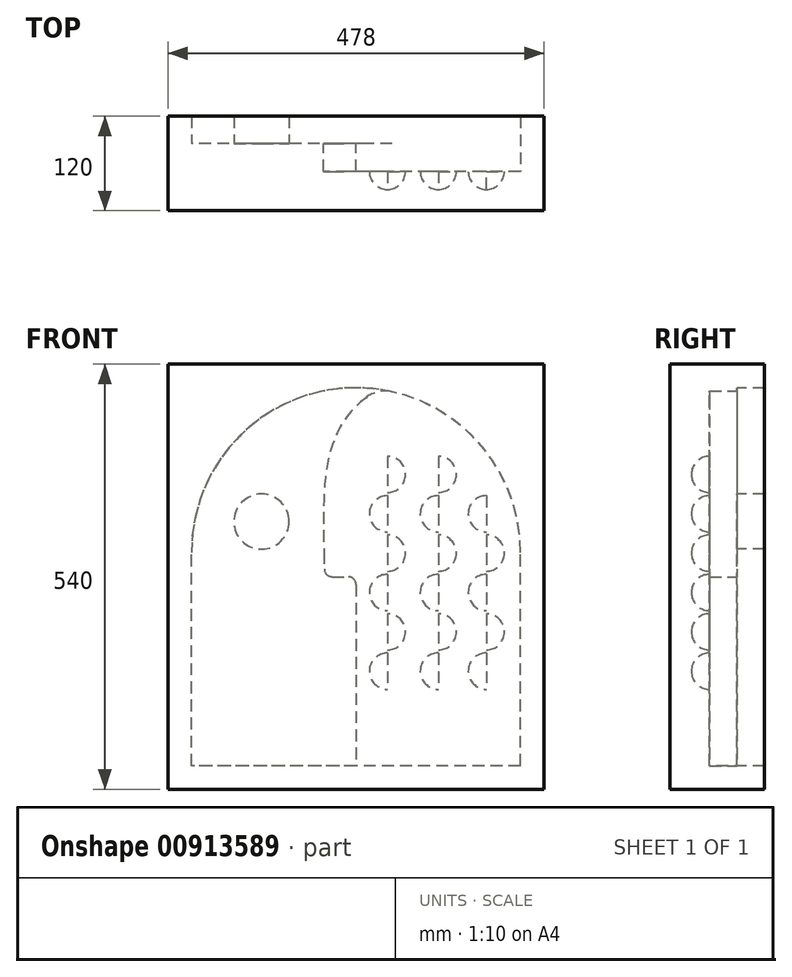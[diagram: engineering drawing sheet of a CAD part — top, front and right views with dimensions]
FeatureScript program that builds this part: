
annotation { "Feature Type Name" : "Feature", "Feature Type Description" : "" }
export const myFeature = defineFeature(function(context is Context, id is Id, definition is map)
    precondition{}
    {
        {
            var Q0;
            Q0=qCreatedBy(makeId("Front.planeOp"),FACE);
            var sketch = newSketch(context, id + "F0", { "sketchPlane" : qUnion([Q0])});
            skLineSegment(sketch, "E0.bottom", {"start": v(209, -110) * mm, "end": v(-209, -110) * mm});
            skLineSegment(sketch, "E0.top", {"start": v(209, 161) * mm, "end": v(-209, 161) * mm});
            skLineSegment(sketch, "E0.left", {"start": v(209, -110) * mm, "end": v(209, 161) * mm});
            skLineSegment(sketch, "E0.right", {"start": v(-209, -110) * mm, "end": v(-209, 161) * mm});
            skPoint(sketch, "E0.middle", {"position": v(0, 25.5) * mm});
            skArc(sketch, "E1", {"start": v(209, 161) * mm, "mid": v(0, 370) * mm, "end": v(-209, 161) * mm});
            skPoint(sketch, "E2.2.internal.snap0", {"position": v(0, 370) * mm});
            skFitSpline(sketch, "E3", {"points": [v(27.95, 368.12) * mm, v(-40, 130) * mm], "startDerivative": vector(-229.22, -141.56) * mm, "endDerivative": vector(8.15, -359.94) * mm});
            skLineSegment(sketch, "E4", {"start": v(-40, 130) * mm, "end": v(0, 130) * mm});
            skLineSegment(sketch, "E5", {"start": v(0, 130) * mm, "end": v(0, -110) * mm});
            skSolve(sketch);
        }
        {
            var Q0;
            {var subQ0=sQuery(id+"F0.wireOp",EDGE,"E1");var subQ3=sQuery(id+"F0.wireOp",EDGE,"E3");var subQ5=makeQuery(id+"F0.imprint","INTERSECT",VERTEX,{"derivedFrom":[subQ0,subQ3]});Q0=makeQuery(id+"F0.imprint","IMPRINT",FACE,{"disambiguationData":[TD([[makeQuery(id+"F0.imprint","IMPRINT",EDGE,{"disambiguationData":[TD([[subQ5,-1.0]])],"derivedFrom":subQ3}),1.0]])]});}
            var Q1;
            {var subQ4=sQuery(id+"F0.wireOp",EDGE,"E0.left");Q1=makeQuery(id+"F0.imprint","IMPRINT",FACE,{"disambiguationData":[TD([[makeQuery(id+"F0.imprint","IMPRINT",EDGE,{"derivedFrom":subQ4}),1.0]])]});}
            extrude(context, id + "F1", {"entities" : qUnion([Q0, Q1]), "depth" : 35 * mm, "offsetDistance" : 25 * mm});
        }
        {
            var Q0;
            {var subQ0=sQuery(id+"F0.wireOp",EDGE,"E1");var subQ3=sQuery(id+"F0.wireOp",EDGE,"E3");var subQ5=makeQuery(id+"F0.imprint","INTERSECT",VERTEX,{"derivedFrom":[subQ0,subQ3]});Q0=makeQuery(id+"F0.imprint","IMPRINT",FACE,{"disambiguationData":[TD([[makeQuery(id+"F0.imprint","IMPRINT",EDGE,{"disambiguationData":[TD([[subQ5,-1.0]])],"derivedFrom":subQ3}),-1.0]])]});}
            var Q1;
            {var subQ4=sQuery(id+"F0.wireOp",EDGE,"E0.right");Q1=makeQuery(id+"F0.imprint","IMPRINT",FACE,{"disambiguationData":[TD([[makeQuery(id+"F0.imprint","IMPRINT",EDGE,{"derivedFrom":subQ4}),-1.0]])]});}
            var Q2;
            {var subQ0=sQuery(id+"F0.wireOp",EDGE,"E1");var subQ3=sQuery(id+"F0.wireOp",EDGE,"E3");var subQ5=makeQuery(id+"F0.imprint","INTERSECT",VERTEX,{"derivedFrom":[subQ0,subQ3]});Q2=makeQuery(id+"F0.imprint","IMPRINT",FACE,{"disambiguationData":[TD([[makeQuery(id+"F0.imprint","IMPRINT",EDGE,{"disambiguationData":[TD([[subQ5,-1.0]])],"derivedFrom":subQ3}),1.0]])]});}
            var Q3;
            {var subQ4=sQuery(id+"F0.wireOp",EDGE,"E0.left");Q3=makeQuery(id+"F0.imprint","IMPRINT",FACE,{"disambiguationData":[TD([[makeQuery(id+"F0.imprint","IMPRINT",EDGE,{"derivedFrom":subQ4}),1.0]])]});}
            extrude(context, id + "F2", {"entities" : qUnion([Q0, Q1, Q2, Q3]), "oppositeDirection" : true, "depth" : 35 * mm, "offsetDistance" : 25 * mm});
        }
        {
            var Q0;
            Q0=qCreatedBy(makeId("Front.planeOp"),FACE);
            var sketch = newSketch(context, id + "F3", { "sketchPlane" : qUnion([Q0])});
            skCircle(sketch, "E6", {"center": v(-120, 200) * mm, "radius": 35 * mm});
            skSolve(sketch);
        }
        {
            var Q0;
            Q0 = qSketchRegion(id + "F3", true);
            extrude(context, id + "F4", {"entities" : qUnion([Q0]), "operationType" : NewBodyOperationType.REMOVE, "oppositeDirection" : true, "depth" : 99 * mm, "offsetDistance" : 25 * mm});
        }
        {
            var Q0;
            Q0=makeQuery(id+"F1.opExtrude","SWEPT_EDGE",EDGE,{"disambiguationData":[OSD([sQuery(id+"F0.wireOp",EDGE,"E3"),sQuery(id+"F0.wireOp",EDGE,"E4")])]});
            fillet(context, id + "F5", {"entities" : qUnion([Q0]), "radius" : 10 * mm, "tangentPropagation" : true, "allowEdgeOverflow" : false});
        }
        {
            var Q0;
            Q0=makeQuery(id+"F1.opExtrude","SWEPT_EDGE",EDGE,{"disambiguationData":[OSD([sQuery(id+"F0.wireOp",EDGE,"E4"),sQuery(id+"F0.wireOp",EDGE,"E5")])]});
            fillet(context, id + "F6", {"entities" : qUnion([Q0]), "radius" : 10 * mm, "tangentPropagation" : true, "allowEdgeOverflow" : false});
        }
        {
            var Q0;
            Q0=makeQuery(id+"F1.opExtrude","SWEPT_EDGE",EDGE,{"disambiguationData":[OSD([sQuery(id+"F0.wireOp",EDGE,"E1"),sQuery(id+"F0.wireOp",EDGE,"E3")])]});
            fillet(context, id + "F7", {"entities" : qUnion([Q0]), "radius" : 40 * mm, "tangentPropagation" : true, "allowEdgeOverflow" : false});
        }
        {
            var Q0;
            Q0=makeQuery(id+"F1.opExtrude","CAP_FACE",FACE,{"disambiguationData":[OSD([sQuery(id+"F0.wireOp",EDGE,"E0.bottom"),sQuery(id+"F0.wireOp",EDGE,"E0.left"),sQuery(id+"F0.wireOp",EDGE,"E1"),sQuery(id+"F0.wireOp",EDGE,"E3"),sQuery(id+"F0.wireOp",EDGE,"E4"),sQuery(id+"F0.wireOp",EDGE,"E5")])],"isStart":false});
            var sketch = newSketch(context, id + "F8", { "sketchPlane" : qUnion([Q0])});
            skArc(sketch, "E7", {"start": v(40, 235) * mm, "mid": v(65, 260) * mm, "end": v(40, 285) * mm});
            skArc(sketch, "E8", {"start": v(40, 135) * mm, "mid": v(65, 160) * mm, "end": v(40, 185) * mm});
            skArc(sketch, "E9", {"start": v(40, 35) * mm, "mid": v(65, 60) * mm, "end": v(40, 85) * mm});
            skArc(sketch, "E10", {"start": v(40, 235) * mm, "mid": v(15, 210) * mm, "end": v(40, 185) * mm});
            skArc(sketch, "E11", {"start": v(40, 135) * mm, "mid": v(15, 110) * mm, "end": v(40, 85) * mm});
            skArc(sketch, "E12", {"start": v(40, 35) * mm, "mid": v(15, 10) * mm, "end": v(40, -15) * mm});
            skLineSegment(sketch, "E13", {"start": v(40, 285) * mm, "end": v(40, 235) * mm});
            skLineSegment(sketch, "E14.trimOffspring", {"start": v(40, 210) * mm, "end": v(40, -15) * mm});
            skArc(sketch, "E15", {"start": v(40, 237) * mm, "mid": v(63, 260) * mm, "end": v(40, 283) * mm});
            skArc(sketch, "E16", {"start": v(40, 233) * mm, "mid": v(17, 210) * mm, "end": v(40, 187) * mm});
            skArc(sketch, "E17", {"start": v(40, 137) * mm, "mid": v(63, 160) * mm, "end": v(40, 183) * mm});
            skArc(sketch, "E18", {"start": v(40, 133) * mm, "mid": v(17, 110) * mm, "end": v(40, 87) * mm});
            skArc(sketch, "E19", {"start": v(40, 37) * mm, "mid": v(63, 60) * mm, "end": v(40, 83) * mm});
            skArc(sketch, "E20", {"start": v(40, 33) * mm, "mid": v(17, 10) * mm, "end": v(40, -13) * mm});
            skPoint(sketch, "E21", {"position": v(40, 283) * mm});
            skPoint(sketch, "E22", {"position": v(40, 237) * mm});
            skPoint(sketch, "E23", {"position": v(40, 233) * mm});
            skPoint(sketch, "E24", {"position": v(40, 187) * mm});
            skPoint(sketch, "E25", {"position": v(40, -13) * mm});
            skPoint(sketch, "E26", {"position": v(40, 33) * mm});
            skPoint(sketch, "E27", {"position": v(40, 37) * mm});
            skPoint(sketch, "E28", {"position": v(40, 83) * mm});
            skPoint(sketch, "E28.positionSnap0", {"position": v(40, 97.5) * mm});
            skPoint(sketch, "E29", {"position": v(40, 87) * mm});
            skPoint(sketch, "E30", {"position": v(40, 133) * mm});
            skLineSegment(sketch, "E31", {"start": v(40, 210) * mm, "end": v(40, 233) * mm});
            skArc(sketch, "E32", {"start": v(104.55, 235) * mm, "mid": v(129.55, 260) * mm, "end": v(104.55, 285) * mm});
            skArc(sketch, "E33", {"start": v(104.55, 135) * mm, "mid": v(129.55, 160) * mm, "end": v(104.55, 185) * mm});
            skArc(sketch, "E34", {"start": v(104.55, 35) * mm, "mid": v(129.55, 60) * mm, "end": v(104.55, 85) * mm});
            skArc(sketch, "E35", {"start": v(104.55, 235) * mm, "mid": v(79.55, 210) * mm, "end": v(104.55, 185) * mm});
            skArc(sketch, "E36", {"start": v(104.55, 135) * mm, "mid": v(79.55, 110) * mm, "end": v(104.55, 85) * mm});
            skArc(sketch, "E37", {"start": v(104.55, 35) * mm, "mid": v(79.55, 10) * mm, "end": v(104.55, -15) * mm});
            skLineSegment(sketch, "E38", {"start": v(104.55, 285) * mm, "end": v(104.55, 235) * mm});
            skLineSegment(sketch, "E39.trimOffspring", {"start": v(104.55, 210) * mm, "end": v(104.55, -15) * mm});
            skArc(sketch, "E40", {"start": v(104.55, 237) * mm, "mid": v(127.55, 260) * mm, "end": v(104.55, 283) * mm});
            skArc(sketch, "E41", {"start": v(104.55, 233) * mm, "mid": v(81.55, 210) * mm, "end": v(104.55, 187) * mm});
            skArc(sketch, "E42", {"start": v(104.55, 137) * mm, "mid": v(127.55, 160) * mm, "end": v(104.55, 183) * mm});
            skArc(sketch, "E43", {"start": v(104.55, 133) * mm, "mid": v(81.55, 110) * mm, "end": v(104.55, 87) * mm});
            skArc(sketch, "E44", {"start": v(104.55, 37) * mm, "mid": v(127.55, 60) * mm, "end": v(104.55, 83) * mm});
            skArc(sketch, "E45", {"start": v(104.55, 33) * mm, "mid": v(81.55, 10) * mm, "end": v(104.55, -13) * mm});
            skPoint(sketch, "E46", {"position": v(104.55, 283) * mm});
            skPoint(sketch, "E47", {"position": v(104.55, 237) * mm});
            skPoint(sketch, "E48", {"position": v(104.55, 233) * mm});
            skPoint(sketch, "E49", {"position": v(104.55, 187) * mm});
            skPoint(sketch, "E50", {"position": v(104.55, -13) * mm});
            skPoint(sketch, "E51", {"position": v(104.55, 33) * mm});
            skPoint(sketch, "E52", {"position": v(104.55, 37) * mm});
            skPoint(sketch, "E53", {"position": v(104.55, 83) * mm});
            skPoint(sketch, "E53.positionSnap0", {"position": v(104.55, 97.5) * mm});
            skPoint(sketch, "E54", {"position": v(104.55, 87) * mm});
            skPoint(sketch, "E55", {"position": v(104.55, 133) * mm});
            skLineSegment(sketch, "E56", {"start": v(104.55, 210) * mm, "end": v(104.55, 233) * mm});
            skArc(sketch, "E57", {"start": v(165.55, 135) * mm, "mid": v(190.55, 160) * mm, "end": v(165.55, 185) * mm});
            skArc(sketch, "E58", {"start": v(165.55, 35) * mm, "mid": v(190.55, 60) * mm, "end": v(165.55, 85) * mm});
            skArc(sketch, "E59", {"start": v(165.55, 235) * mm, "mid": v(140.55, 210) * mm, "end": v(165.55, 185) * mm});
            skArc(sketch, "E60", {"start": v(165.55, 135) * mm, "mid": v(140.55, 110) * mm, "end": v(165.55, 85) * mm});
            skArc(sketch, "E61", {"start": v(165.55, 35) * mm, "mid": v(140.55, 10) * mm, "end": v(165.55, -15) * mm});
            skLineSegment(sketch, "E62.trimOffspring", {"start": v(165.55, 210) * mm, "end": v(165.55, -15) * mm});
            skArc(sketch, "E63", {"start": v(165.55, 233) * mm, "mid": v(142.55, 210) * mm, "end": v(165.55, 187) * mm});
            skArc(sketch, "E64", {"start": v(165.55, 137) * mm, "mid": v(188.55, 160) * mm, "end": v(165.55, 183) * mm});
            skArc(sketch, "E65", {"start": v(165.55, 133) * mm, "mid": v(142.55, 110) * mm, "end": v(165.55, 87) * mm});
            skArc(sketch, "E66", {"start": v(165.55, 37) * mm, "mid": v(188.55, 60) * mm, "end": v(165.55, 83) * mm});
            skArc(sketch, "E67", {"start": v(165.55, 33) * mm, "mid": v(142.55, 10) * mm, "end": v(165.55, -13) * mm});
            skPoint(sketch, "E68", {"position": v(165.55, 237) * mm});
            skPoint(sketch, "E69", {"position": v(165.55, 233) * mm});
            skPoint(sketch, "E70", {"position": v(165.55, 187) * mm});
            skPoint(sketch, "E71", {"position": v(165.55, -13) * mm});
            skPoint(sketch, "E72", {"position": v(165.55, 33) * mm});
            skPoint(sketch, "E73", {"position": v(165.55, 37) * mm});
            skPoint(sketch, "E74", {"position": v(165.55, 83) * mm});
            skPoint(sketch, "E74.positionSnap0", {"position": v(165.55, 97.5) * mm});
            skPoint(sketch, "E75", {"position": v(165.55, 87) * mm});
            skPoint(sketch, "E76", {"position": v(165.55, 133) * mm});
            skLineSegment(sketch, "E77", {"start": v(165.55, 210) * mm, "end": v(165.55, 233) * mm});
            skSolve(sketch);
        }
        {
            var Q0;
            {var subQ0=sQuery(id+"F8.wireOp",EDGE,"E15");Q0=makeQuery(id+"F8.imprint","IMPRINT",FACE,{"disambiguationData":[TD([[makeQuery(id+"F8.imprint","IMPRINT",EDGE,{"derivedFrom":subQ0}),1.0]])]});}
            var Q1;
            {var subQ2=sQuery(id+"F8.wireOp",EDGE,"E16");Q1=makeQuery(id+"F8.imprint","IMPRINT",FACE,{"disambiguationData":[TD([[makeQuery(id+"F8.imprint","IMPRINT",EDGE,{"derivedFrom":subQ2}),1.0]])]});}
            var Q2;
            {var subQ0=sQuery(id+"F8.wireOp",EDGE,"E17");Q2=makeQuery(id+"F8.imprint","IMPRINT",FACE,{"disambiguationData":[TD([[makeQuery(id+"F8.imprint","IMPRINT",EDGE,{"derivedFrom":subQ0}),1.0]])]});}
            var Q3;
            {var subQ0=sQuery(id+"F8.wireOp",EDGE,"E18");Q3=makeQuery(id+"F8.imprint","IMPRINT",FACE,{"disambiguationData":[TD([[makeQuery(id+"F8.imprint","IMPRINT",EDGE,{"derivedFrom":subQ0}),1.0]])]});}
            var Q4;
            {var subQ0=sQuery(id+"F8.wireOp",EDGE,"E19");Q4=makeQuery(id+"F8.imprint","IMPRINT",FACE,{"disambiguationData":[TD([[makeQuery(id+"F8.imprint","IMPRINT",EDGE,{"derivedFrom":subQ0}),1.0]])]});}
            var Q5;
            {var subQ0=sQuery(id+"F8.wireOp",EDGE,"E20");Q5=makeQuery(id+"F8.imprint","IMPRINT",FACE,{"disambiguationData":[TD([[makeQuery(id+"F8.imprint","IMPRINT",EDGE,{"derivedFrom":subQ0}),1.0]])]});}
            var Q6;
            {var subQ0=sQuery(id+"F8.wireOp",EDGE,"E40");Q6=makeQuery(id+"F8.imprint","IMPRINT",FACE,{"disambiguationData":[TD([[makeQuery(id+"F8.imprint","IMPRINT",EDGE,{"derivedFrom":subQ0}),1.0]])]});}
            var Q7;
            {var subQ2=sQuery(id+"F8.wireOp",EDGE,"E41");Q7=makeQuery(id+"F8.imprint","IMPRINT",FACE,{"disambiguationData":[TD([[makeQuery(id+"F8.imprint","IMPRINT",EDGE,{"derivedFrom":subQ2}),1.0]])]});}
            var Q8;
            {var subQ0=sQuery(id+"F8.wireOp",EDGE,"E42");Q8=makeQuery(id+"F8.imprint","IMPRINT",FACE,{"disambiguationData":[TD([[makeQuery(id+"F8.imprint","IMPRINT",EDGE,{"derivedFrom":subQ0}),1.0]])]});}
            var Q9;
            {var subQ0=sQuery(id+"F8.wireOp",EDGE,"E43");Q9=makeQuery(id+"F8.imprint","IMPRINT",FACE,{"disambiguationData":[TD([[makeQuery(id+"F8.imprint","IMPRINT",EDGE,{"derivedFrom":subQ0}),1.0]])]});}
            var Q10;
            {var subQ0=sQuery(id+"F8.wireOp",EDGE,"E44");Q10=makeQuery(id+"F8.imprint","IMPRINT",FACE,{"disambiguationData":[TD([[makeQuery(id+"F8.imprint","IMPRINT",EDGE,{"derivedFrom":subQ0}),1.0]])]});}
            var Q11;
            {var subQ0=sQuery(id+"F8.wireOp",EDGE,"E45");Q11=makeQuery(id+"F8.imprint","IMPRINT",FACE,{"disambiguationData":[TD([[makeQuery(id+"F8.imprint","IMPRINT",EDGE,{"derivedFrom":subQ0}),1.0]])]});}
            var Q12;
            {var subQ0=sQuery(id+"F8.wireOp",EDGE,"7c425a16-0659-460d-bd44-7cd90c1e36e4");Q12=makeQuery(id+"F8.imprint","IMPRINT",FACE,{"disambiguationData":[TD([[makeQuery(id+"F8.imprint","IMPRINT",EDGE,{"derivedFrom":subQ0}),1.0]])]});}
            var Q13;
            {var subQ0=sQuery(id+"F8.wireOp",EDGE,"73a80a7e-780d-446c-98ed-7b7f9ac50c4b");Q13=makeQuery(id+"F8.imprint","IMPRINT",FACE,{"disambiguationData":[TD([[makeQuery(id+"F8.imprint","IMPRINT",EDGE,{"derivedFrom":subQ0}),1.0]])]});}
            var Q14;
            {var subQ0=sQuery(id+"F8.wireOp",EDGE,"810e4cb4-5b06-4c2a-ad52-313fb0827d73");Q14=makeQuery(id+"F8.imprint","IMPRINT",FACE,{"disambiguationData":[TD([[makeQuery(id+"F8.imprint","IMPRINT",EDGE,{"derivedFrom":subQ0}),1.0]])]});}
            var Q15;
            {var subQ0=sQuery(id+"F8.wireOp",EDGE,"32e1f96f-e752-4156-bb51-bfc9b94aef00");Q15=makeQuery(id+"F8.imprint","IMPRINT",FACE,{"disambiguationData":[TD([[makeQuery(id+"F8.imprint","IMPRINT",EDGE,{"derivedFrom":subQ0}),1.0]])]});}
            var Q16;
            {var subQ2=sQuery(id+"F8.wireOp",EDGE,"cbac5d50-3c56-4f29-aa4d-7e592c7854ca");Q16=makeQuery(id+"F8.imprint","IMPRINT",FACE,{"disambiguationData":[TD([[makeQuery(id+"F8.imprint","IMPRINT",EDGE,{"derivedFrom":subQ2}),1.0]])]});}
            var Q17;
            {var subQ2=sQuery(id+"F8.wireOp",EDGE,"E63");Q17=makeQuery(id+"F8.imprint","IMPRINT",FACE,{"disambiguationData":[TD([[makeQuery(id+"F8.imprint","IMPRINT",EDGE,{"derivedFrom":subQ2}),1.0]])]});}
            var Q18;
            {var subQ0=sQuery(id+"F8.wireOp",EDGE,"E64");Q18=makeQuery(id+"F8.imprint","IMPRINT",FACE,{"disambiguationData":[TD([[makeQuery(id+"F8.imprint","IMPRINT",EDGE,{"derivedFrom":subQ0}),1.0]])]});}
            var Q19;
            {var subQ0=sQuery(id+"F8.wireOp",EDGE,"E65");Q19=makeQuery(id+"F8.imprint","IMPRINT",FACE,{"disambiguationData":[TD([[makeQuery(id+"F8.imprint","IMPRINT",EDGE,{"derivedFrom":subQ0}),1.0]])]});}
            var Q20;
            {var subQ0=sQuery(id+"F8.wireOp",EDGE,"E66");Q20=makeQuery(id+"F8.imprint","IMPRINT",FACE,{"disambiguationData":[TD([[makeQuery(id+"F8.imprint","IMPRINT",EDGE,{"derivedFrom":subQ0}),1.0]])]});}
            var Q21;
            {var subQ0=sQuery(id+"F8.wireOp",EDGE,"E67");Q21=makeQuery(id+"F8.imprint","IMPRINT",FACE,{"disambiguationData":[TD([[makeQuery(id+"F8.imprint","IMPRINT",EDGE,{"derivedFrom":subQ0}),1.0]])]});}
            var Q22;
            {var subQ0=sQuery(id+"F8.wireOp",EDGE,"f0158336-0400-4b4a-9e41-d58de429e5bc");Q22=makeQuery(id+"F8.imprint","IMPRINT",FACE,{"disambiguationData":[TD([[makeQuery(id+"F8.imprint","IMPRINT",EDGE,{"derivedFrom":subQ0}),1.0]])]});}
            var Q23;
            Q23=makeQuery(id+"F8.imprint","IMPRINT",FACE,{"disambiguationData":[TD([[makeQuery(id+"F8.imprint","IMPRINT",EDGE,{"derivedFrom":sQuery(id+"F8.wireOp",EDGE,"8be67b42-60bf-458d-a955-e76f2ad68274")}),1.0]])]});
            extrude(context, id + "F9", {"entities" : qUnion([Q0, Q1, Q2, Q3, Q4, Q5, Q6, Q7, Q8, Q9, Q10, Q11, Q12, Q13, Q14, Q15, Q16, Q17, Q18, Q19, Q20, Q21, Q22, Q23]), "operationType" : NewBodyOperationType.ADD, "depth" : 23 * mm, "offsetDistance" : 25 * mm});
        }
        {
            var Q0;
            Q0=makeQuery(id+"F9.opExtrude","CAP_EDGE",EDGE,{"disambiguationData":[OSD([sQuery(id+"F8.wireOp",EDGE,"E15")])],"isStart":false});
            var Q1;
            Q1=makeQuery(id+"F9.opExtrude","CAP_EDGE",EDGE,{"disambiguationData":[OSD([sQuery(id+"F8.wireOp",EDGE,"E16")])],"isStart":false});
            var Q2;
            Q2=makeQuery(id+"F9.opExtrude","CAP_EDGE",EDGE,{"disambiguationData":[OSD([sQuery(id+"F8.wireOp",EDGE,"E17")])],"isStart":false});
            var Q3;
            Q3=makeQuery(id+"F9.opExtrude","CAP_EDGE",EDGE,{"disambiguationData":[OSD([sQuery(id+"F8.wireOp",EDGE,"E18")])],"isStart":false});
            var Q4;
            Q4=makeQuery(id+"F9.opExtrude","CAP_EDGE",EDGE,{"disambiguationData":[OSD([sQuery(id+"F8.wireOp",EDGE,"E19")])],"isStart":false});
            var Q5;
            Q5=makeQuery(id+"F9.opExtrude","CAP_EDGE",EDGE,{"disambiguationData":[OSD([sQuery(id+"F8.wireOp",EDGE,"E20")])],"isStart":false});
            var Q6;
            Q6=makeQuery(id+"F9.opExtrude","CAP_EDGE",EDGE,{"disambiguationData":[OSD([sQuery(id+"F8.wireOp",EDGE,"E45")])],"isStart":false});
            var Q7;
            Q7=makeQuery(id+"F9.opExtrude","CAP_EDGE",EDGE,{"disambiguationData":[OSD([sQuery(id+"F8.wireOp",EDGE,"E44")])],"isStart":false});
            var Q8;
            Q8=makeQuery(id+"F9.opExtrude","CAP_EDGE",EDGE,{"disambiguationData":[OSD([sQuery(id+"F8.wireOp",EDGE,"E43")])],"isStart":false});
            var Q9;
            Q9=makeQuery(id+"F9.opExtrude","CAP_EDGE",EDGE,{"disambiguationData":[OSD([sQuery(id+"F8.wireOp",EDGE,"E42")])],"isStart":false});
            var Q10;
            Q10=makeQuery(id+"F9.opExtrude","CAP_EDGE",EDGE,{"disambiguationData":[OSD([sQuery(id+"F8.wireOp",EDGE,"E41")])],"isStart":false});
            var Q11;
            Q11=makeQuery(id+"F9.opExtrude","CAP_EDGE",EDGE,{"disambiguationData":[OSD([sQuery(id+"F8.wireOp",EDGE,"E40")])],"isStart":false});
            var Q12;
            Q12=makeQuery(id+"F9.opExtrude","CAP_EDGE",EDGE,{"disambiguationData":[OSD([sQuery(id+"F8.wireOp",EDGE,"cbac5d50-3c56-4f29-aa4d-7e592c7854ca")])],"isStart":false});
            var Q13;
            Q13=makeQuery(id+"F9.opExtrude","CAP_EDGE",EDGE,{"disambiguationData":[OSD([sQuery(id+"F8.wireOp",EDGE,"810e4cb4-5b06-4c2a-ad52-313fb0827d73")])],"isStart":false});
            var Q14;
            Q14=makeQuery(id+"F9.opExtrude","CAP_EDGE",EDGE,{"disambiguationData":[OSD([sQuery(id+"F8.wireOp",EDGE,"7c425a16-0659-460d-bd44-7cd90c1e36e4")])],"isStart":false});
            var Q15;
            Q15=makeQuery(id+"F9.opExtrude","CAP_EDGE",EDGE,{"disambiguationData":[OSD([sQuery(id+"F8.wireOp",EDGE,"E63")])],"isStart":false});
            var Q16;
            Q16=makeQuery(id+"F9.opExtrude","CAP_EDGE",EDGE,{"disambiguationData":[OSD([sQuery(id+"F8.wireOp",EDGE,"E64")])],"isStart":false});
            var Q17;
            Q17=makeQuery(id+"F9.opExtrude","CAP_EDGE",EDGE,{"disambiguationData":[OSD([sQuery(id+"F8.wireOp",EDGE,"E65")])],"isStart":false});
            var Q18;
            Q18=makeQuery(id+"F9.opExtrude","CAP_EDGE",EDGE,{"disambiguationData":[OSD([sQuery(id+"F8.wireOp",EDGE,"E66")])],"isStart":false});
            var Q19;
            Q19=makeQuery(id+"F9.opExtrude","CAP_EDGE",EDGE,{"disambiguationData":[OSD([sQuery(id+"F8.wireOp",EDGE,"E67")])],"isStart":false});
            var Q20;
            Q20=makeQuery(id+"F9.opExtrude","CAP_EDGE",EDGE,{"disambiguationData":[OSD([sQuery(id+"F8.wireOp",EDGE,"f0158336-0400-4b4a-9e41-d58de429e5bc")])],"isStart":false});
            var Q21;
            Q21=makeQuery(id+"F9.opExtrude","CAP_EDGE",EDGE,{"disambiguationData":[OSD([sQuery(id+"F8.wireOp",EDGE,"8be67b42-60bf-458d-a955-e76f2ad68274")])],"isStart":false});
            fillet(context, id + "F10", {"entities" : qUnion([Q0, Q1, Q2, Q3, Q4, Q5, Q6, Q7, Q8, Q9, Q10, Q11, Q12, Q13, Q14, Q15, Q16, Q17, Q18, Q19, Q20, Q21]), "radius" : 23 * mm, "tangentPropagation" : true, "allowEdgeOverflow" : false});
        }
        {
            var Q0;
            Q0=makeQuery(id+"F2.opExtrude","SWEPT_BODY",BODY,{"disambiguationData":[OSD([sQuery(id+"F0.wireOp",EDGE,"E0.bottom"),sQuery(id+"F0.wireOp",EDGE,"E0.left"),sQuery(id+"F0.wireOp",EDGE,"E0.right"),sQuery(id+"F0.wireOp",EDGE,"E1")])]});
            var Q1;
            Q1=makeQuery(id+"F1.opExtrude","SWEPT_BODY",BODY,{"disambiguationData":[OSD([sQuery(id+"F0.wireOp",EDGE,"E0.bottom"),sQuery(id+"F0.wireOp",EDGE,"E0.left"),sQuery(id+"F0.wireOp",EDGE,"E1"),sQuery(id+"F0.wireOp",EDGE,"E3"),sQuery(id+"F0.wireOp",EDGE,"E4"),sQuery(id+"F0.wireOp",EDGE,"E5")])]});
            booleanBodies(context, id + "F11", {"operationType" : BooleanOperationType.UNION, "tools" : qUnion([Q0, Q1])});
        }
        {
            var Q0;
            Q0=makeQuery(id+"F2.opExtrude","CAP_FACE",FACE,{"disambiguationData":[OSD([sQuery(id+"F0.wireOp",EDGE,"E0.bottom"),sQuery(id+"F0.wireOp",EDGE,"E0.left"),sQuery(id+"F0.wireOp",EDGE,"E0.right"),sQuery(id+"F0.wireOp",EDGE,"E1")])],"isStart":false});
            var sketch = newSketch(context, id + "F12", { "sketchPlane" : qUnion([Q0])});
            skLineSegment(sketch, "E78.bottom", {"start": v(-239, 400) * mm, "end": v(239, 400) * mm});
            skLineSegment(sketch, "E78.top", {"start": v(-239, -140) * mm, "end": v(239, -140) * mm});
            skLineSegment(sketch, "E78.left", {"start": v(-239, 400) * mm, "end": v(-239, -140) * mm});
            skLineSegment(sketch, "E78.right", {"start": v(239, 400) * mm, "end": v(239, -140) * mm});
            skSolve(sketch);
        }
        {
            var Q0;
            Q0 = qSketchRegion(id + "F12", true);
            extrude(context, id + "F13", {"entities" : qUnion([Q0]), "oppositeDirection" : true, "depth" : 120 * mm, "offsetDistance" : 25 * mm});
        }
        {
            var Q0;
            Q0=makeQuery(id+"F2.opExtrude","SWEPT_BODY",BODY,{"disambiguationData":[OSD([sQuery(id+"F0.wireOp",EDGE,"E0.bottom"),sQuery(id+"F0.wireOp",EDGE,"E0.left"),sQuery(id+"F0.wireOp",EDGE,"E0.right"),sQuery(id+"F0.wireOp",EDGE,"E1")])]});
            var Q1;
            Q1=makeQuery(id+"F13.opExtrude","SWEPT_BODY",BODY,{"disambiguationData":[OSD([sQuery(id+"F12.wireOp",EDGE,"E78.bottom"),sQuery(id+"F12.wireOp",EDGE,"E78.top"),sQuery(id+"F12.wireOp",EDGE,"E78.left"),sQuery(id+"F12.wireOp",EDGE,"E78.right")])]});
            booleanBodies(context, id + "F14", {"operationType" : BooleanOperationType.SUBTRACTION, "tools" : qUnion([Q0]), "targets" : qUnion([Q1])});
        }
    });
